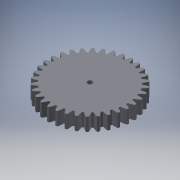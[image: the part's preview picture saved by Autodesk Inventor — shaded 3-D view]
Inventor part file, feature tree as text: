
AUTODESK INVENTOR PART (.ipt)
format: ipt  version: 2016 (Build 200138000, 138)  size: 275,968 bytes
history: native  units: mm (DEFAULTED — no unit token found)
features: plane x3, other x3, sketch x3, extrude x2
ambient origin geometry x8: Origin, YZ Plane, XZ Plane, XY Plane, X Axis, Y Axis, Z Axis, Center Point
bodies: Solid1 (feature_tree)
feature tree (11):
  extrude  "Extrusion1"  Depth=15.0mm TaperAngle=0.0deg
  plane  "Work Plane2"
  plane  "Work Plane8"
  plane  "Work Plane9"
  other  "Spur Gear"
  extrude  "Extrusion2"  Depth=10.0mm TaperAngle=0.0deg
  sketch  "Sketch1"  dims[d0=95.4mm d1=15.0mm d2=0.0mm]
  sketch  "Sketch2"  dims[d3=90.1mm d4=10.0mm d5=0.0mm]
  other  "Srf1"
  sketch  "Sketch3"  dims[d16=180.2mm d17=0.0mm d34=0.923998mm d39=0.0mm d41=0.0mm d43=180.2mm d46=180.2mm d47=0.0mm d48=0.0mm d49=5.5mm d50=10.0mm d51=0.0mm]
  other  "Pitch Diameter"
